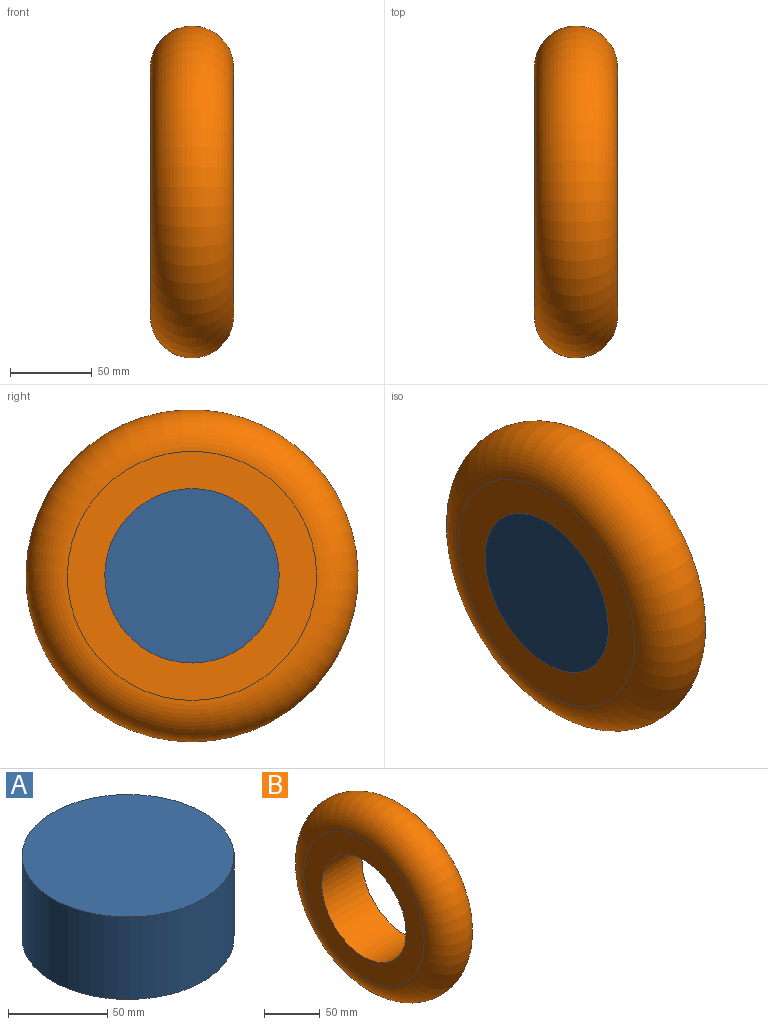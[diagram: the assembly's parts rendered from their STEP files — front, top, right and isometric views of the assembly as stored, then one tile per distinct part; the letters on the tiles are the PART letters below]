
ASSEMBLY  parts=2 mates=1
PART A: 3 faces, bbox 106.7x106.7x50.8 mm
  f0: cylinder r=53.34mm len=106.68mm, axis (0,0,-1), area 17025.4mm2, adj f1,f2
  f1: plane 106.68x106.68mm, normal (0,0,1), area 8938.3mm2, adj f0
  f2: plane 106.68x106.68mm, normal (0,0,-1), area 8938.3mm2, adj f0
PART B: 4 faces, bbox 50.8x219.9x219.9 mm
  f0: plane 152.4x152.4mm, normal (1,0,0), area 9303.1mm2, adj f2,f3
  f1: plane 152.4x152.4mm, normal (-1,0,0), area 9303.1mm2, adj f2,f3
  f2: cylinder r=53.34mm len=106.68mm, axis (1,0,0), area 17025.4mm2, adj f0,f1
  f3: torus R=76.2mm, axis (1,0,0), area 46312.2mm2, adj f0,f1
PLACE A rot(axis=(0,1,0),90deg) t=(-97.31,-90.37,-154.59)mm
PLACE B t=(-97.31,-90.37,29.55)mm
MATE fastened A.f0 <-> B.f2  axis (1,0,0) through (-46.51,-90.37,29.55)mm
